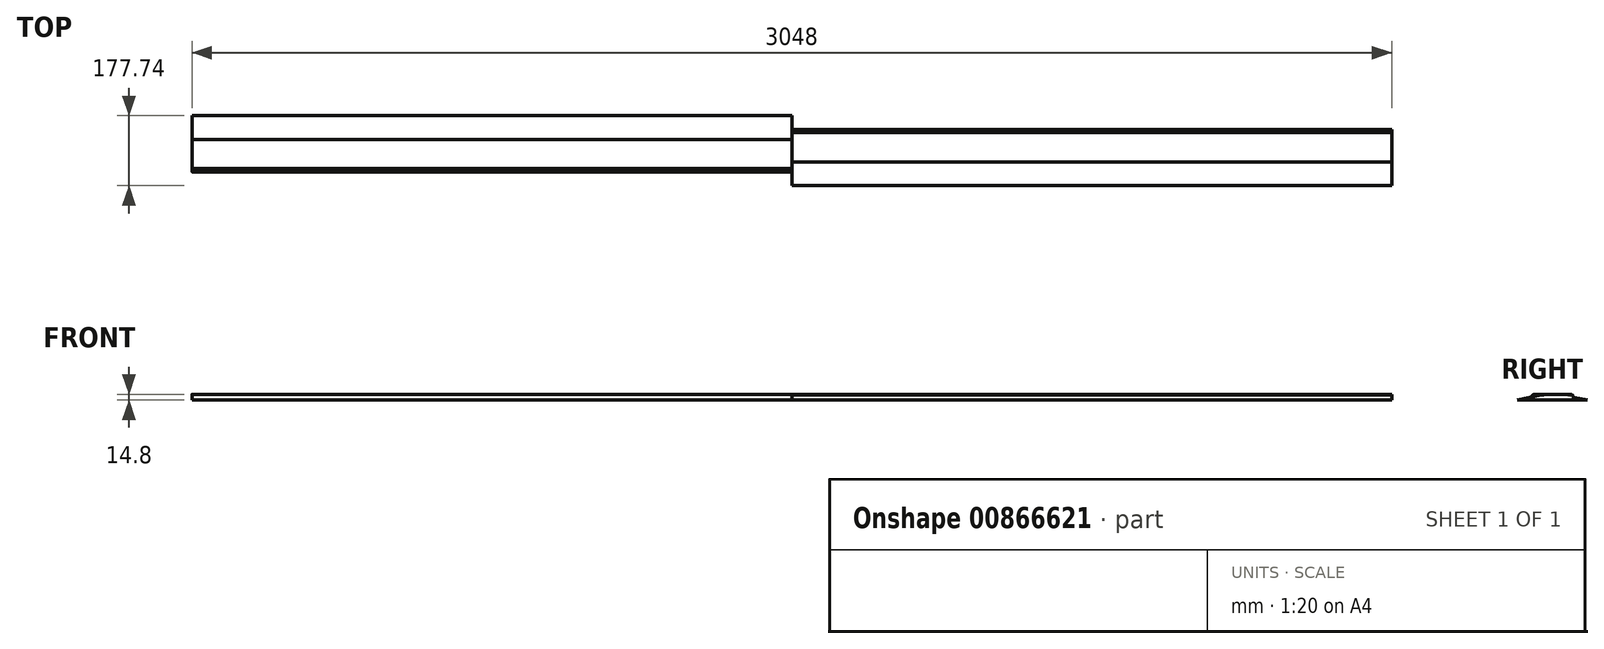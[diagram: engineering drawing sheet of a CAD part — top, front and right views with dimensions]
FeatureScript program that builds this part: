
annotation { "Feature Type Name" : "Feature", "Feature Type Description" : "" }
export const myFeature = defineFeature(function(context is Context, id is Id, definition is map)
    precondition{}
    {
        {
            var Q0;
            Q0=qCreatedBy(makeId("Right.planeOp"),FACE);
            var sketch = newSketch(context, id + "F0", { "sketchPlane" : qUnion([Q0])});
            skLineSegment(sketch, "E0", {"start": v(88.87, 54.32) * mm, "end": v(28.44, 66.92) * mm});
            skFitSpline(sketch, "E1", {"points": [v(28.44, 66.92) * mm, v(17.03, 68.5) * mm, v(-45.76, 68.89) * mm], "startDerivative": vector(-30.32, 5.95) * mm, "endDerivative": vector(-107.76, -1.08) * mm});
            skLineSegment(sketch, "E2", {"start": v(88.87, 54.32) * mm, "end": v(-48.32, 54.32) * mm});
            skArc(sketch, "E3", {"start": v(-45.76, 68.89) * mm, "mid": v(-53.37, 62.72) * mm, "end": v(-48.32, 54.32) * mm});
            skSolve(sketch);
        }
        {
            var Q0;
            Q0 = qSketchRegion(id + "F0", true);
            extrude(context, id + "F1", {"entities" : qUnion([Q0]), "oppositeDirection" : true, "depth" : 1524 * mm, "offsetDistance" : 25.4 * mm});
        }
        {
            var Q0;
            Q0=qCreatedBy(makeId("Top.planeOp"),FACE);
            var sketch = newSketch(context, id + "F2", { "sketchPlane" : qUnion([Q0])});
            skCircle(sketch, "E4", {"center": v(0, 0) * mm, "radius": 63.96 * mm});
            skSolve(sketch);
        }
        {
            var Q0;
            Q0=makeQuery(id+"F1.opExtrude","SWEPT_BODY",BODY,{"disambiguationData":[OSD([sQuery(id+"F0.wireOp",EDGE,"E0"),sQuery(id+"F0.wireOp",EDGE,"E1"),sQuery(id+"F0.wireOp",EDGE,"E2"),sQuery(id+"F0.wireOp",EDGE,"E3")])]});
            var Q1;
            Q1=sQuery(id+"F2.wireOp",EDGE,"E4");
            circularPattern(context, id + "F3", {"entities" : qUnion([Q0]), "axis" : qUnion([Q1]), "angle" : 360 * degree, "instanceCount" : 2, "equalSpace" : true});
        }
    });
